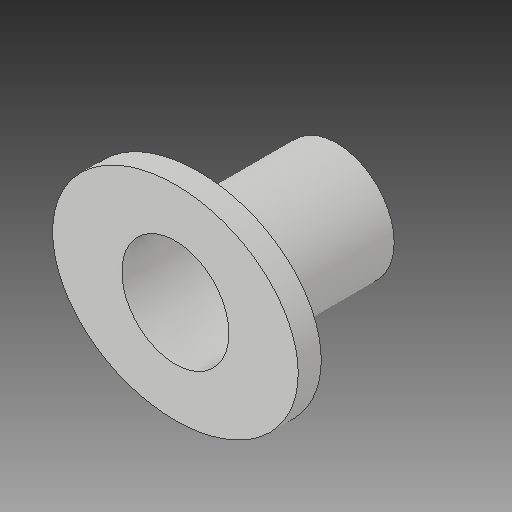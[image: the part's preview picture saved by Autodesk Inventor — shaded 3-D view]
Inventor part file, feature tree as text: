
AUTODESK INVENTOR PART (.ipt)
format: ipt  version: 2017 (Build 210142000, 142)  size: 104,960 bytes
history: native  units: mm
features: sketch x4, other x3
ambient origin geometry x8: Origin, YZ Plane, XZ Plane, XY Plane, X Axis, Y Axis, Z Axis, Center Point
bodies: Solid1 (feature_tree)
feature tree (7):
  other  "Pushfit-adapter-cap_MIR.ipt"
  other  "Solid1::Pushfit-adapter-cap_MIR.ipt"
  other  "TaggingFeature1"
  sketch  "Sketch1"  dims[d0=10.0mm]
  sketch  "Sketch2"
  sketch  "Sketch3"
  sketch  "Sketch4"
